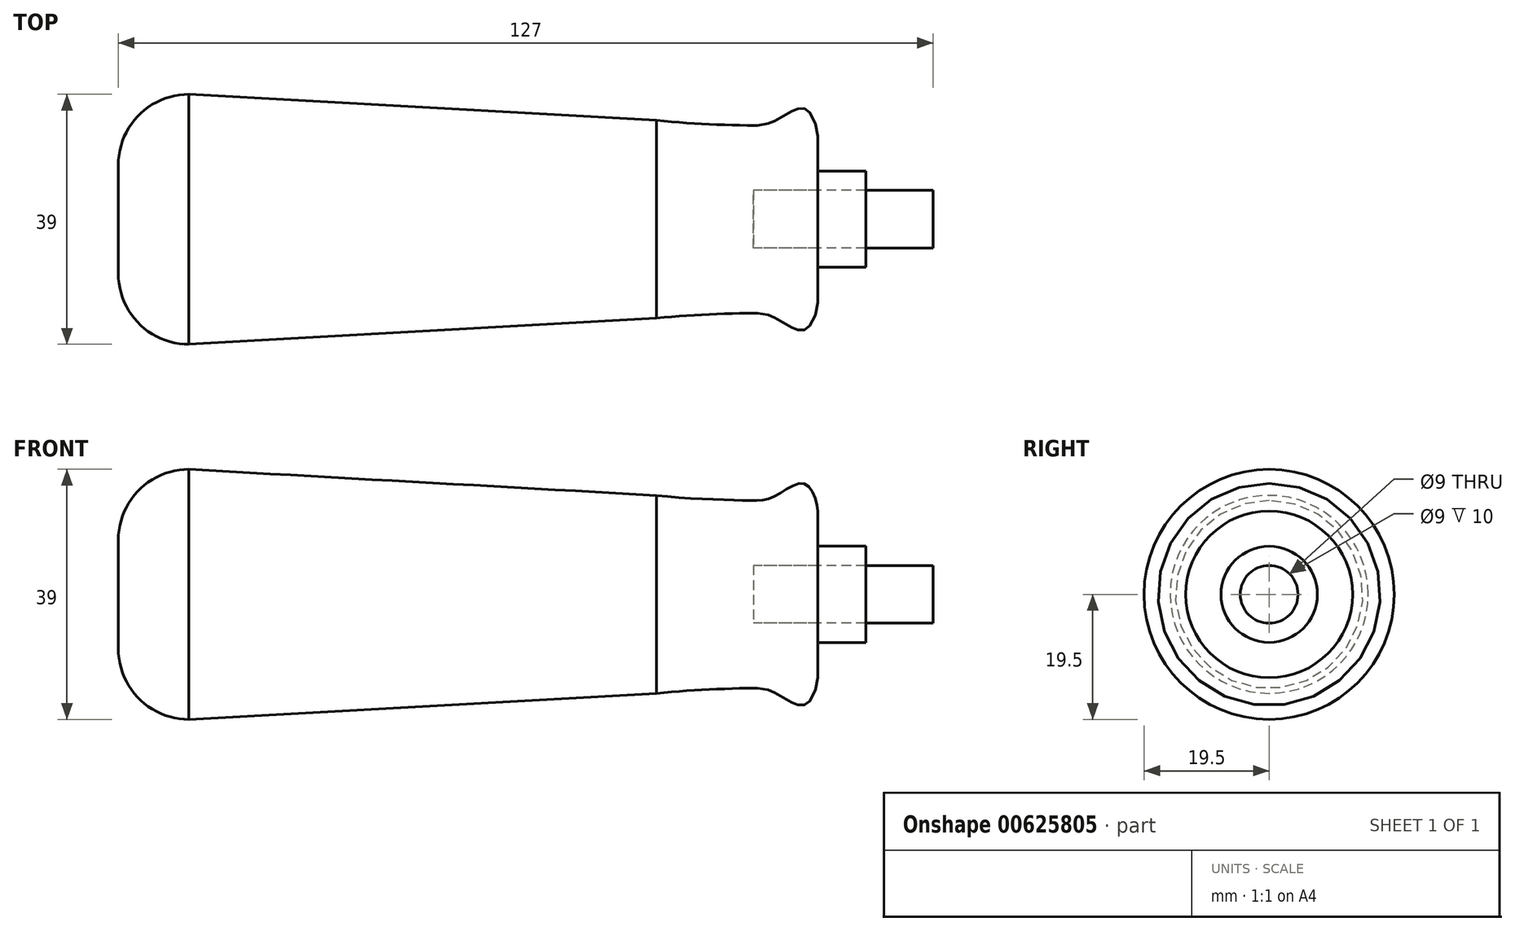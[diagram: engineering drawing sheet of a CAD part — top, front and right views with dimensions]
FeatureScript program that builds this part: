
annotation { "Feature Type Name" : "Feature", "Feature Type Description" : "" }
export const myFeature = defineFeature(function(context is Context, id is Id, definition is map)
    precondition{}
    {
        {
            var Q0;
            Q0=qCreatedBy(makeId("Front.planeOp"),FACE);
            var sketch = newSketch(context, id + "F0", { "sketchPlane" : qUnion([Q0])});
            skLineSegment(sketch, "E0", {"start": v(0, 0) * mm, "end": v(126, 0) * mm});
            skPoint(sketch, "E1", {"position": v(11, 0) * mm});
            skLineSegment(sketch, "E2", {"start": v(11, 19.5) * mm, "end": v(83.89, 15.43) * mm});
            skLineSegment(sketch, "E3", {"start": v(11, 0) * mm, "end": v(11, 26.57) * mm, "construction": true});
            skLineSegment(sketch, "E4", {"start": v(-24.26, 0) * mm, "end": v(99, 0) * mm, "construction": true});
            skLineSegment(sketch, "E5", {"start": v(109, 13) * mm, "end": v(109, 4.5) * mm});
            skLineSegment(sketch, "E6", {"start": v(109, 4.5) * mm, "end": v(99, 4.5) * mm});
            skLineSegment(sketch, "E7", {"start": v(99, 4.5) * mm, "end": v(99, 0) * mm});
            skPoint(sketch, "E8.orphan", {"position": v(109, 0) * mm});
            skLineSegment(sketch, "E9.trimOffspring", {"start": v(109, 0) * mm, "end": v(151.94, 0) * mm, "construction": true});
            skLineSegment(sketch, "E10", {"start": v(0, 0) * mm, "end": v(0, 8.5) * mm});
            skArc(sketch, "E11", {"start": v(0, 8.5) * mm, "mid": v(3.22, 16.28) * mm, "end": v(11, 19.5) * mm});
            skFitSpline(sketch, "E12", {"points": [v(83.89, 15.43) * mm, v(97.67, 14.64) * mm, v(102.34, 15.35) * mm, v(107.08, 17.22) * mm, v(109, 13) * mm], "startDerivative": vector(38.5, -4.28) * mm, "endDerivative": vector(1.14, -17.09) * mm});
            skSolve(sketch);
        }
        {
            var Q0;
            Q0 = qSketchRegion(id + "F0", true);
            var Q1;
            Q1=sQuery(id+"F0.wireOp",EDGE,"E9.trimOffspring");
            revolve(context, id + "F1", {"entities" : qUnion([Q0]), "axis" : qUnion([Q1]), "revolveType" : RevolveType.FULL});
        }
        {
            var Q0;
            Q0=qCreatedBy(makeId("Front.planeOp"),FACE);
            var sketch = newSketch(context, id + "F2", { "sketchPlane" : qUnion([Q0])});
            skLineSegment(sketch, "E13", {"start": v(109, 4.5) * mm, "end": v(116.5, 4.5) * mm});
            skLineSegment(sketch, "E14", {"start": v(116.5, 4.5) * mm, "end": v(116.5, 7.5) * mm});
            skLineSegment(sketch, "E15", {"start": v(116.5, 7.5) * mm, "end": v(109, 7.5) * mm});
            skLineSegment(sketch, "E16", {"start": v(109, 7.5) * mm, "end": v(109, 4.5) * mm});
            skSolve(sketch);
        }
        {
            var Q0;
            Q0=makeQuery(id+"F2.imprint","IMPRINT",FACE,{"disambiguationData":[TD([[makeQuery(id+"F2.imprint","IMPRINT",EDGE,{"derivedFrom":sQuery(id+"F2.wireOp",EDGE,"E13")}),1.0]])]});
            var Q1;
            Q1=sQuery(id+"F0.wireOp",EDGE,"E9.trimOffspring");
            revolve(context, id + "F3", {"entities" : qUnion([Q0]), "axis" : qUnion([Q1]), "revolveType" : RevolveType.FULL});
        }
        {
            var Q0;
            Q0=makeQuery(id+"F1.opRevolve","SWEPT_FACE",FACE,{"disambiguationData":[OSD([sQuery(id+"F0.wireOp",EDGE,"E7")])]});
            var sketch = newSketch(context, id + "F4", { "sketchPlane" : qUnion([Q0])});
            skCircle(sketch, "E17.0", {"center": v(0, 0) * mm, "radius": 4.5 * mm});
            skSolve(sketch);
        }
        {
            var Q0;
            Q0 = qSketchRegion(id + "F4", true);
            extrude(context, id + "F5", {"entities" : qUnion([Q0]), "depth" : 28 * mm, "offsetDistance" : 25 * mm});
        }
    });
